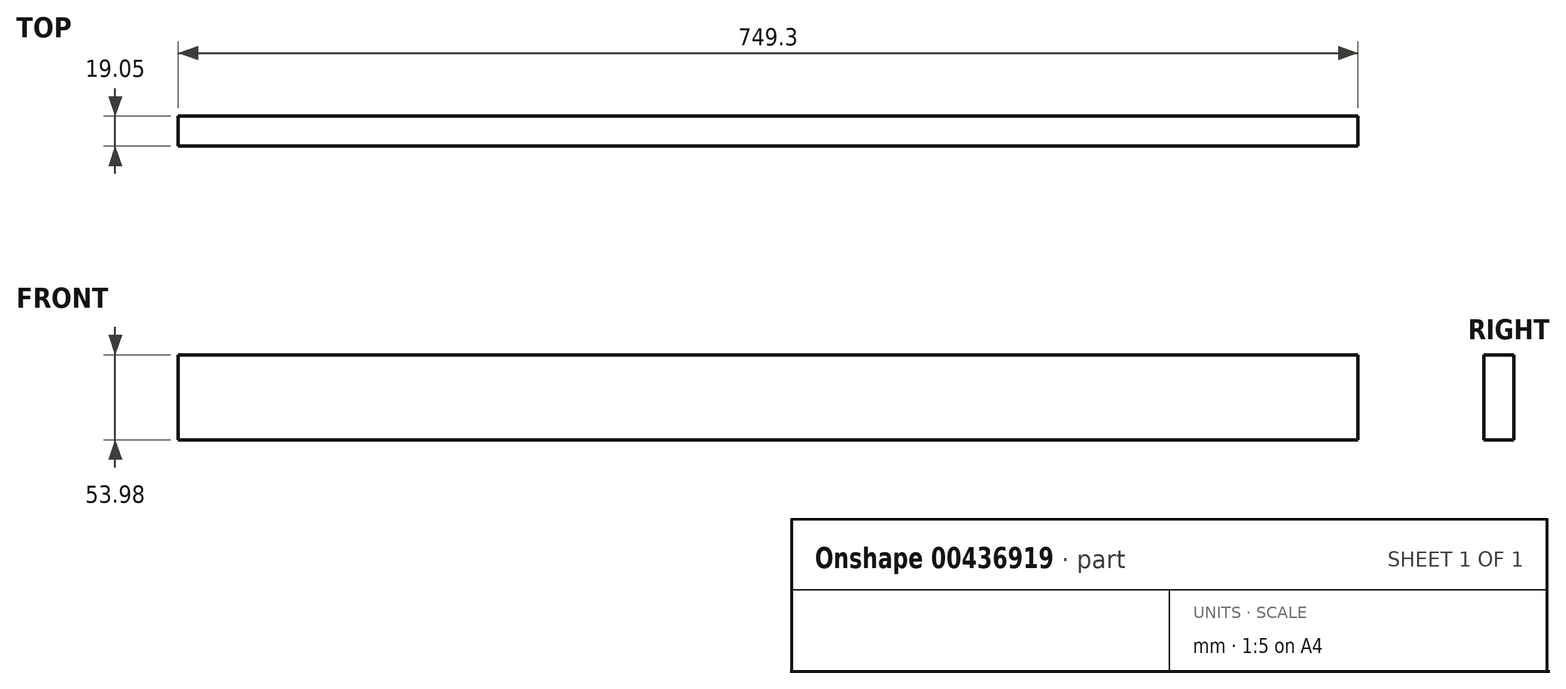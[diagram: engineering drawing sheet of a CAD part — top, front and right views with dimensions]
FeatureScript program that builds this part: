
annotation { "Feature Type Name" : "Feature", "Feature Type Description" : "" }
export const myFeature = defineFeature(function(context is Context, id is Id, definition is map)
    precondition{}
    {
        {
            var Q0;
            Q0=qCreatedBy(makeId("Front.planeOp"),FACE);
            var sketch = newSketch(context, id + "F0", { "sketchPlane" : qUnion([Q0])});
            skLineSegment(sketch, "E0.bottom", {"start": v(0, 0) * mm, "end": v(749.3, 0) * mm});
            skLineSegment(sketch, "E0.top", {"start": v(0, 53.98) * mm, "end": v(749.3, 53.98) * mm});
            skLineSegment(sketch, "E0.left", {"start": v(0, 0) * mm, "end": v(0, 53.98) * mm});
            skLineSegment(sketch, "E0.right", {"start": v(749.3, 0) * mm, "end": v(749.3, 53.98) * mm});
            skSolve(sketch);
        }
        {
            var Q0;
            Q0=makeQuery(id+"F0.imprint","IMPRINT",FACE,{"disambiguationData":[TD([[makeQuery(id+"F0.imprint","IMPRINT",EDGE,{"derivedFrom":sQuery(id+"F0.wireOp",EDGE,"E0.bottom")}),1.0]])]});
            extrude(context, id + "F1", {"entities" : qUnion([Q0]), "depth" : 19.05 * mm});
        }
    });
